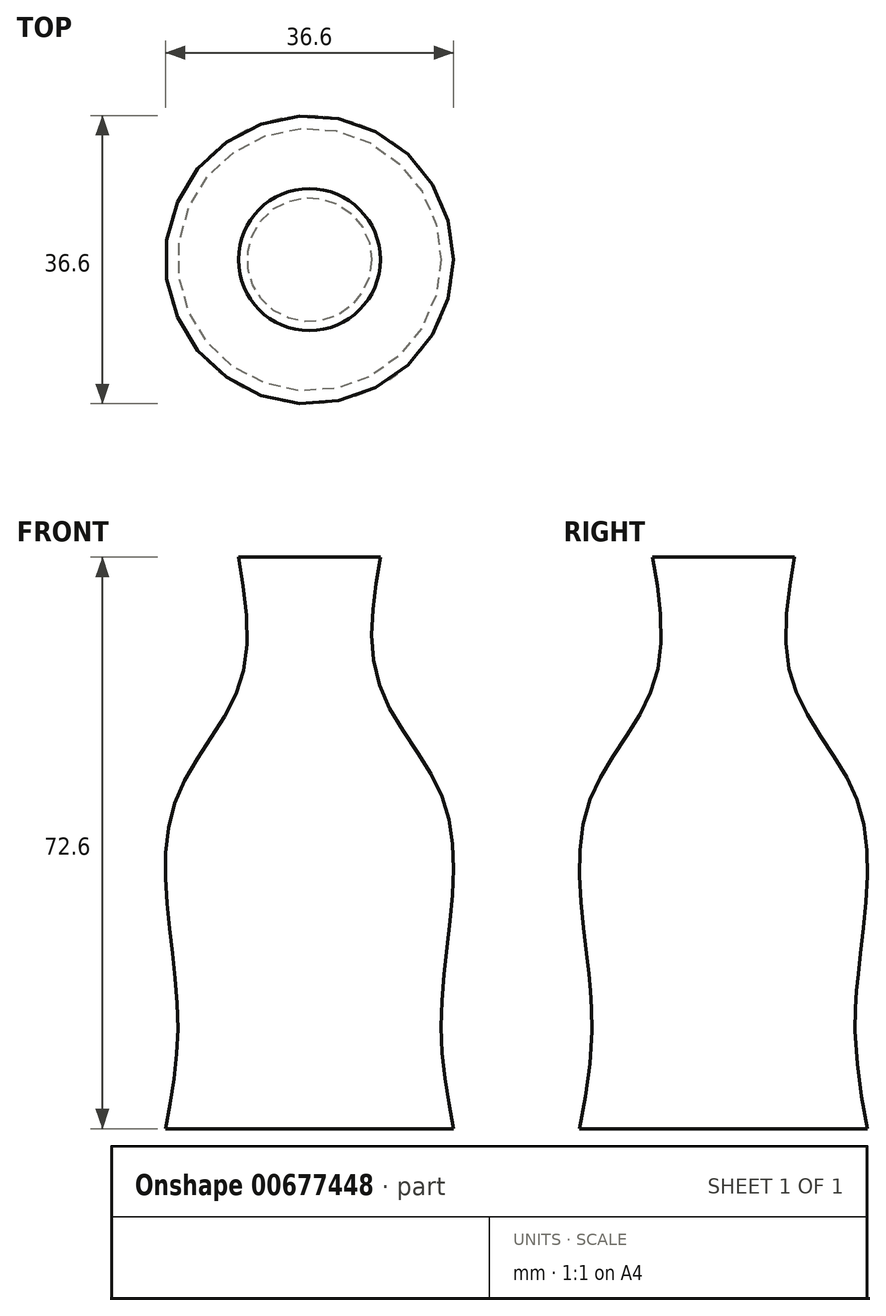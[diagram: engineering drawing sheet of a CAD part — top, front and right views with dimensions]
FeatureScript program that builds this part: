
annotation { "Feature Type Name" : "Feature", "Feature Type Description" : "" }
export const myFeature = defineFeature(function(context is Context, id is Id, definition is map)
    precondition{}
    {
        {
            var Q0;
            Q0=qCreatedBy(makeId("Top.planeOp"),FACE);
            var sketch = newSketch(context, id + "F0", { "sketchPlane" : qUnion([Q0])});
            skCircle(sketch, "E0", {"center": v(0, 0) * mm, "radius": 18.27 * mm});
            skSolve(sketch);
        }
        {
            var Q0;
            Q0=qCreatedBy(makeId("Top.planeOp"),FACE);
            cPlane(context, id + "F1", {"entities" : qUnion([Q0]), "cplaneType" : CPlaneType.OFFSET, "offset" : 57.2 * mm, "width" : 150 * mm, "height" : 150 * mm});
        }
        {
            var Q0;
            Q0=qCreatedBy(id+"F1.planeOp",FACE);
            var sketch = newSketch(context, id + "F2", { "sketchPlane" : qUnion([Q0])});
            skCircle(sketch, "E1", {"center": v(0, 0) * mm, "radius": 8.63 * mm});
            skSolve(sketch);
        }
        {
            var Q0;
            Q0=qCreatedBy(makeId("Top.planeOp"),FACE);
            cPlane(context, id + "F3", {"entities" : qUnion([Q0]), "cplaneType" : CPlaneType.OFFSET, "offset" : 12.5 * mm, "width" : 150 * mm, "height" : 150 * mm});
        }
        {
            var Q0;
            Q0=qCreatedBy(id+"F3.planeOp",FACE);
            cPlane(context, id + "F4", {"entities" : qUnion([Q0]), "cplaneType" : CPlaneType.OFFSET, "offset" : 30.2 * mm, "width" : 150 * mm, "height" : 150 * mm});
        }
        {
            var Q0;
            Q0=qCreatedBy(id+"F3.planeOp",FACE);
            cPlane(context, id + "F5", {"entities" : qUnion([Q0]), "cplaneType" : CPlaneType.OFFSET, "offset" : 42.3 * mm, "width" : 150 * mm, "height" : 150 * mm});
        }
        {
            var Q0;
            Q0=qCreatedBy(id+"F3.planeOp",FACE);
            cPlane(context, id + "F6", {"entities" : qUnion([Q0]), "cplaneType" : CPlaneType.OFFSET, "offset" : 60.1 * mm, "width" : 150 * mm, "height" : 150 * mm});
        }
        {
            var Q0;
            Q0=qCreatedBy(id+"F3.planeOp",FACE);
            var sketch = newSketch(context, id + "F7", { "sketchPlane" : qUnion([Q0])});
            skCircle(sketch, "E2", {"center": v(0, 0) * mm, "radius": 16.7 * mm});
            skSolve(sketch);
        }
        {
            var Q0;
            Q0=qCreatedBy(id+"F4.planeOp",FACE);
            var sketch = newSketch(context, id + "F8", { "sketchPlane" : qUnion([Q0])});
            skCircle(sketch, "E3", {"center": v(0, 0) * mm, "radius": 16.62 * mm});
            skSolve(sketch);
        }
        {
            var Q0;
            Q0=qCreatedBy(id+"F5.planeOp",FACE);
            var sketch = newSketch(context, id + "F9", { "sketchPlane" : qUnion([Q0])});
            skCircle(sketch, "E4", {"center": v(0, 0) * mm, "radius": 9.52 * mm});
            skSolve(sketch);
        }
        {
            var Q0;
            Q0=qCreatedBy(id+"F6.planeOp",FACE);
            var sketch = newSketch(context, id + "F10", { "sketchPlane" : qUnion([Q0])});
            skCircle(sketch, "E5", {"center": v(0, 0) * mm, "radius": 9.02 * mm});
            skSolve(sketch);
        }
        {
            var Q0;
            Q0=makeQuery(id+"F0.imprint","IMPRINT",FACE,{"disambiguationData":[TD([[makeQuery(id+"F0.imprint","IMPRINT",EDGE,{"derivedFrom":sQuery(id+"F0.wireOp",EDGE,"E0")}),1.0]])]});
            var Q1;
            Q1=makeQuery(id+"F7.imprint","IMPRINT",FACE,{"disambiguationData":[TD([[makeQuery(id+"F7.imprint","IMPRINT",EDGE,{"derivedFrom":sQuery(id+"F7.wireOp",EDGE,"E2")}),1.0]])]});
            var Q2;
            Q2=makeQuery(id+"F8.imprint","IMPRINT",FACE,{"disambiguationData":[TD([[makeQuery(id+"F8.imprint","IMPRINT",EDGE,{"derivedFrom":sQuery(id+"F8.wireOp",EDGE,"E3")}),1.0]])]});
            var Q3;
            Q3=makeQuery(id+"F9.imprint","IMPRINT",FACE,{"disambiguationData":[TD([[makeQuery(id+"F9.imprint","IMPRINT",EDGE,{"derivedFrom":sQuery(id+"F9.wireOp",EDGE,"E4")}),1.0]])]});
            var Q4;
            Q4=makeQuery(id+"F2.imprint","IMPRINT",FACE,{"disambiguationData":[TD([[makeQuery(id+"F2.imprint","IMPRINT",EDGE,{"derivedFrom":sQuery(id+"F2.wireOp",EDGE,"E1")}),1.0]])]});
            var Q5;
            Q5=makeQuery(id+"F10.imprint","IMPRINT",FACE,{"disambiguationData":[TD([[makeQuery(id+"F10.imprint","IMPRINT",EDGE,{"derivedFrom":sQuery(id+"F10.wireOp",EDGE,"E5")}),1.0]])]});
            loft(context, id + "F11", {"sheetProfilesArray" : [{ "sheetProfileEntities" : qUnion([Q0]) }, { "sheetProfileEntities" : qUnion([Q1]) }, { "sheetProfileEntities" : qUnion([Q2]) }, { "sheetProfileEntities" : qUnion([Q3]) }, { "sheetProfileEntities" : qUnion([Q4]) }, { "sheetProfileEntities" : qUnion([Q5]) }]});
        }
    });
